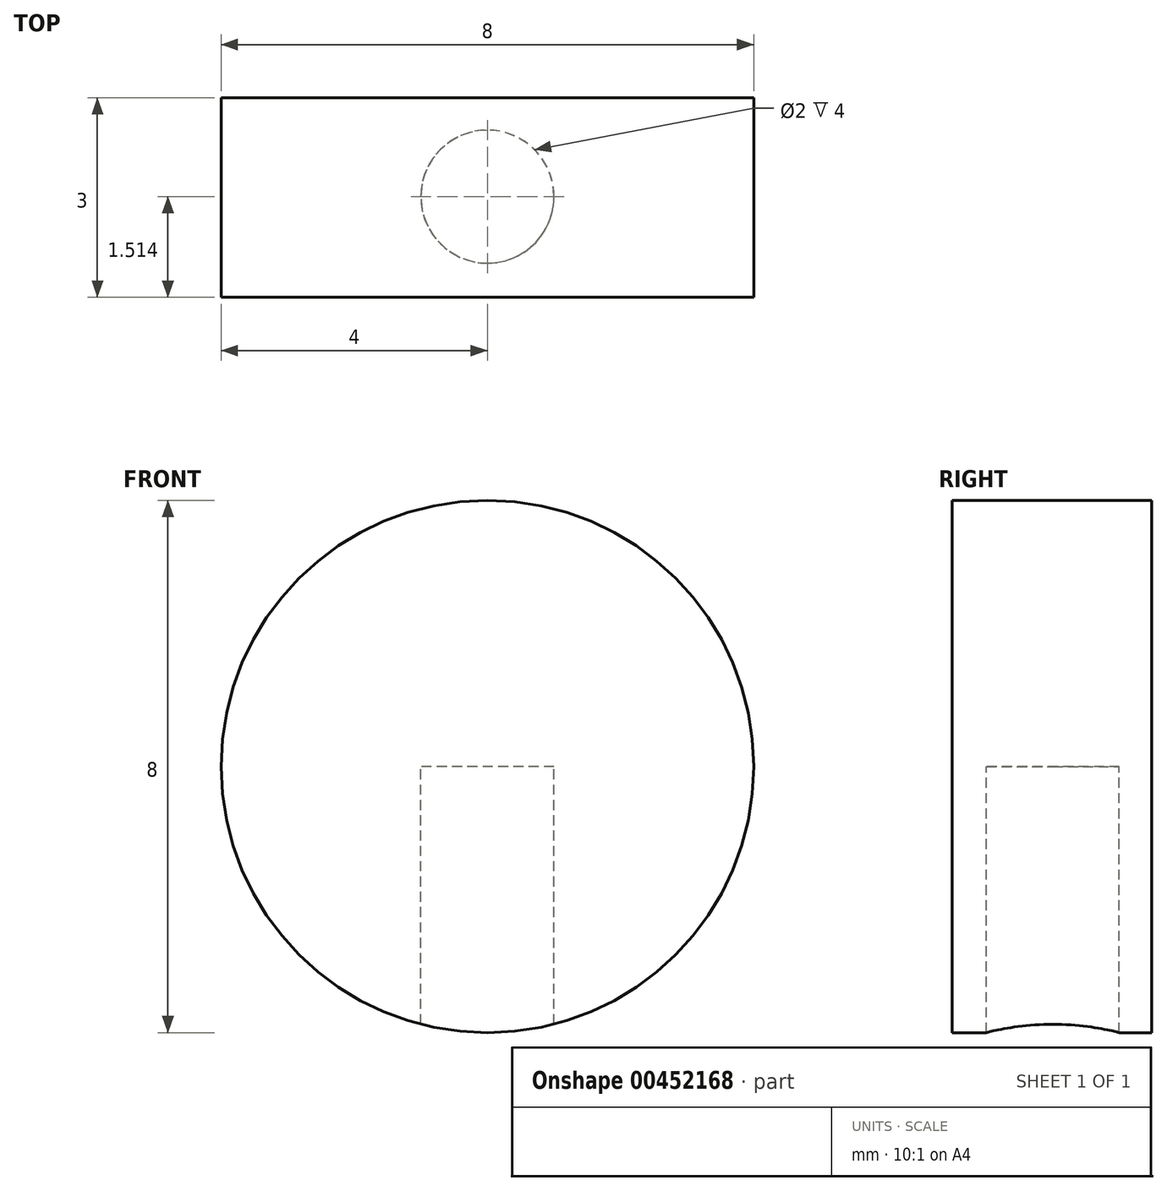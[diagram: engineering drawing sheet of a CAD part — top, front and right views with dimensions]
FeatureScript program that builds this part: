
annotation { "Feature Type Name" : "Feature", "Feature Type Description" : "" }
export const myFeature = defineFeature(function(context is Context, id is Id, definition is map)
    precondition{}
    {
        {
            var Q0;
            Q0=qCreatedBy(makeId("Front.planeOp"),FACE);
            var sketch = newSketch(context, id + "F0", { "sketchPlane" : qUnion([Q0])});
            skCircle(sketch, "E0", {"center": v(0, 0) * mm, "radius": 4 * mm});
            skSolve(sketch);
        }
        {
            var Q0;
            Q0 = qSketchRegion(id + "F0", true);
            extrude(context, id + "F1", {"entities" : qUnion([Q0]), "depth" : 3 * mm});
        }
        {
            var Q0;
            Q0=qCreatedBy(makeId("Top.planeOp"),FACE);
            var sketch = newSketch(context, id + "F2", { "sketchPlane" : qUnion([Q0])});
            skCircle(sketch, "E1", {"center": v(0, -1.49) * mm, "radius": 1 * mm});
            skSolve(sketch);
        }
        {
            var Q0;
            Q0 = qSketchRegion(id + "F2", true);
            extrude(context, id + "F3", {"entities" : qUnion([Q0]), "operationType" : NewBodyOperationType.REMOVE, "oppositeDirection" : true, "depth" : 5 * mm});
        }
    });
